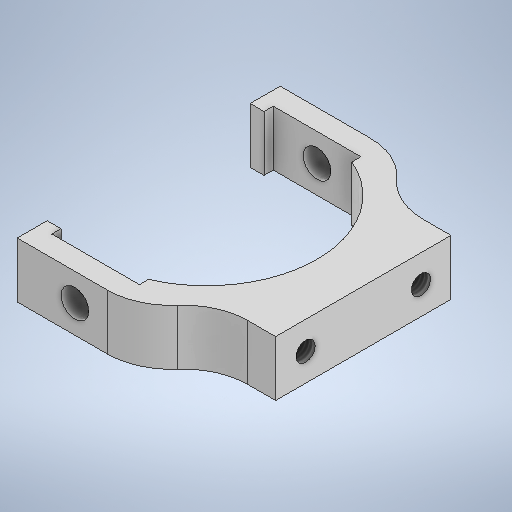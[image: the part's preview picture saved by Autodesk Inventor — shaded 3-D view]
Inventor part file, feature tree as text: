
AUTODESK INVENTOR PART (.ipt)
format: ipt  version: 2025.1 (Build 291241000, 241)  size: 329,728 bytes
history: native  units: mm
features: sketch x3, hole x2, extrude x1, mirror x1
ambient origin geometry x8: Origin, YZ Plane, XZ Plane, XY Plane, X Axis, Y Axis, Z Axis, Center Point
bodies: Solid1 (feature_tree)
feature tree (7):
  extrude  "Extrusion1"  Depth=9.5mm
  hole  "Hole1"  [1 undecoded]
  hole  "Hole2"  [1 undecoded]
  mirror  "Mirror1"
  sketch  "Sketch1"  dims[d0=48.0mm d1=9.5mm]
  sketch  "Sketch2"  dims[d2=9.5mm d3=38.0mm]
  sketch  "Sketch3"  dims[d4=19.0mm d5=14.0mm d7=14.0mm d8=14.0mm d9=14.0mm d10=7.0mm d11=14.0mm d12=7.0mm d13=12.5mm d14=12.5mm d15=4.5mm d16=4.5mm d17=2.0mm d18=2.0mm d19=24.0mm d20=24.0mm d21=6.0mm d22=12.0mm d23=0.0mm d24=4.134mm d25=10.0mm d26=4.0mm d27=2.0mm d28=90.0deg d29=8.0mm d30=20.594885mm d31=25.0mm d32=12.5mm d33=6.0mm d34=10.0mm d35=4.0mm d36=2.0mm d37=90.0deg d38=8.0mm d39=0.0mm d40=12.5mm]
note: 2 required parameter values undecoded (feature->parameter linkage not recoverable at this tier; creation-order binding heuristic only, values carry confidence <= 0.55)
